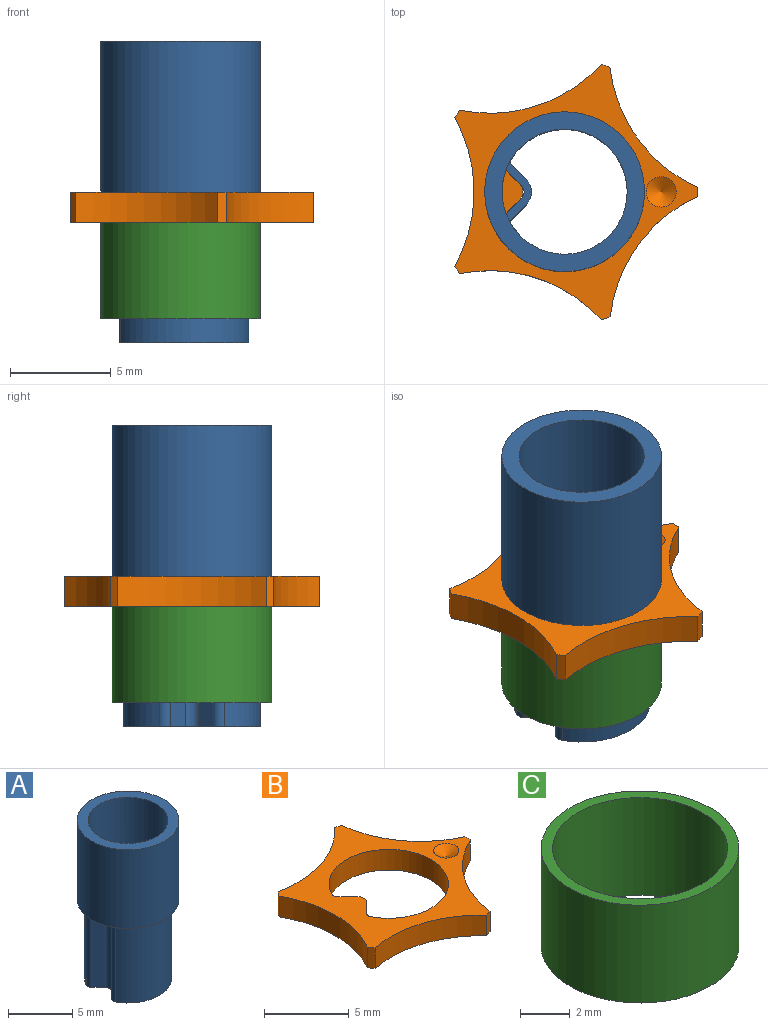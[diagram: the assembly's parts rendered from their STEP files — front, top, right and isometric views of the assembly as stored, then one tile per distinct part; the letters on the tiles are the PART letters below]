
ASSEMBLY  parts=3 mates=2
PART A: 17 faces, bbox 7.9x7.9x15 mm
  f0: cylinder r=3.11mm len=15mm, axis (0,0,-1), area 268.3mm2, adj f2,f3,f4,f14,f15,f16
  f1: cylinder r=3.97mm len=7.94mm, axis (0,0,-1), area 187.1mm2, adj f2,f3
  f2: plane 7.94x7.94mm, normal (0,0,1), area 19.2mm2, adj f0,f1
  f3: plane 7.94x7.94mm, normal (0,0,-1), area 14mm2, adj f0,f1,f9,f10,f11
  f4: cylinder r=0.15mm len=7.5mm, axis (0,0,1), area 1.5mm2, adj f0,f5,f15,f16
  f5: plane 7.5x0.75mm, normal (0.71,0.71,0), area 7.9mm2, adj f4,f6,f15,f16
  f6: cylinder r=0.9mm len=7.5mm, axis (0,0,1), area 10.6mm2, adj f5,f7,f15,f16
  f7: plane 7.5x0.75mm, normal (0.71,-0.71,0), area 7.9mm2, adj f6,f14,f15,f16
  f8: plane 7.5x0.76mm, normal (-0.71,-0.71,0), area 8.1mm2, adj f9,f13,f15,f16
  f9: cylinder r=0.45mm len=7.5mm, axis (0,0,1), area 4.3mm2, adj f3,f8,f10,f15,f16
  f10: cylinder r=3.4mm len=7.5mm, axis (0,0,1), area 134.8mm2, adj f3,f9,f11,f15
  f11: cylinder r=0.45mm len=7.5mm, axis (0,0,1), area 4.3mm2, adj f3,f10,f12,f15,f16
  f12: plane 7.5x0.76mm, normal (-0.71,0.71,0), area 8.1mm2, adj f11,f13,f15,f16
  f13: cylinder r=0.45mm len=7.5mm, axis (0,0,1), area 5.3mm2, adj f8,f12,f15,f16
  f14: cylinder r=0.15mm len=7.5mm, axis (0,0,1), area 1.5mm2, adj f0,f7,f15,f16
  f15: plane 6.79x6.44mm, normal (0,0,-1), area 6.4mm2, adj f0,f4,f5,f6,f7,f8,f9,f10
  f16: plane 3.13x1.26mm, normal (0,0,1), area 1.3mm2, adj f0,f4,f5,f6,f7,f8,f9,f11
PART B: 19 faces, bbox 12.1x12.7x1.5 mm
  f0: cylinder r=7.5mm len=7.03mm, axis (0,0,-1), area 11.6mm2, adj f1,f15,f16,f17
  f1: cylinder r=6.6mm len=1.5mm, axis (0,0,-1), area 0.7mm2, adj f0,f2,f16,f17
  f2: cylinder r=7.5mm len=7.39mm, axis (0,0,-1), area 11.6mm2, adj f1,f3,f16,f17
  f3: cylinder r=6.6mm len=1.5mm, axis (0,0,-1), area 0.7mm2, adj f2,f4,f16,f17
  f4: cylinder r=7.5mm len=7.02mm, axis (0,0,-1), area 11.6mm2, adj f3,f5,f16,f17
  f5: cylinder r=6.6mm len=1.5mm, axis (0,0,-1), area 0.7mm2, adj f4,f6,f16,f17
  f6: cylinder r=7.5mm len=5.97mm, axis (0,0,-1), area 11.6mm2, adj f5,f7,f16,f17
  f7: cylinder r=6.6mm len=1.5mm, axis (0,0,-1), area 0.7mm2, adj f6,f8,f16,f17
  f8: cylinder r=7.5mm len=5.98mm, axis (0,0,-1), area 11.6mm2, adj f7,f15,f16,f17
  f9: cylinder r=3.53mm len=7.06mm, axis (0,0,-1), area 28.3mm2, adj f10,f14,f16,f17
  f10: cylinder r=0.3mm len=1.5mm, axis (0,0,-1), area 0.6mm2, adj f9,f11,f16,f17
  f11: plane 1.5x0.83mm, normal (0.71,-0.71,0), area 1.8mm2, adj f10,f12,f16,f17
  f12: cylinder r=0.6mm len=1.5mm, axis (0,0,-1), area 1.4mm2, adj f11,f13,f16,f17
  f13: plane 1.5x0.83mm, normal (0.71,0.71,0), area 1.8mm2, adj f12,f14,f16,f17
  f14: cylinder r=0.3mm len=1.5mm, axis (0,0,-1), area 0.6mm2, adj f9,f13,f16,f17
  f15: cylinder r=6.6mm len=1.5mm, axis (0,0,-1), area 0.7mm2, adj f0,f8,f16,f17
  f16: plane 12.69x12.07mm, normal (0,0,1), area 45.8mm2, adj f0,f1,f2,f3,f4,f5,f6,f7
  f17: plane 12.69x12.07mm, normal (0,0,-1), area 47.6mm2, adj f0,f1,f2,f3,f4,f5,f6,f7
  f18: cone r=0.75mm half-angle=60deg, axis (0,0,1), area 2mm2, adj f16
PART C: 4 faces, bbox 7.9x7.9x4.8 mm
  f0: cylinder r=3.51mm len=7.02mm, axis (0,0,-1), area 105.8mm2, adj f2,f3
  f1: cylinder r=3.97mm len=7.94mm, axis (0,0,-1), area 119.7mm2, adj f2,f3
  f2: plane 7.94x7.94mm, normal (0,0,1), area 10.8mm2, adj f0,f1
  f3: plane 7.94x7.94mm, normal (0,0,-1), area 10.8mm2, adj f0,f1
PLACE A at identity fixed
PLACE B t=(0,0,-1.5)mm
PLACE C t=(0,0,-6.3)mm
MATE fastened B.f1 <-> C.f0  axis (0,0,-1) through (0,0,-1.5)mm
MATE fastened A.f0 <-> B.f1  axis (0,0,1) through (0,0,0)mm
